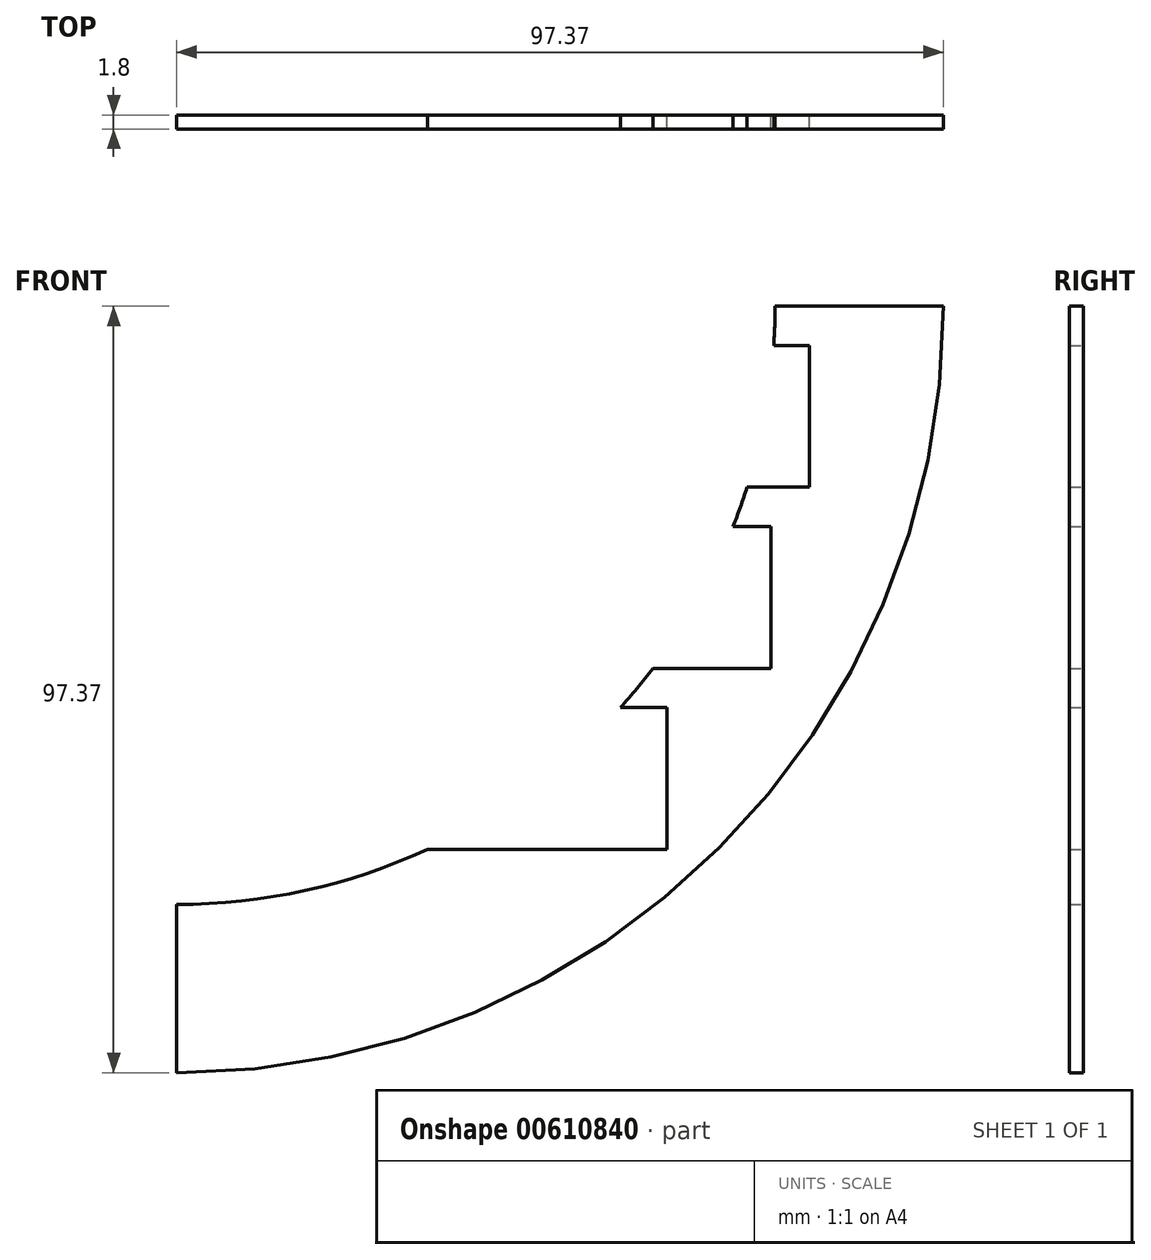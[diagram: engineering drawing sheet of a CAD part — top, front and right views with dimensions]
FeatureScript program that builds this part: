
annotation { "Feature Type Name" : "Feature", "Feature Type Description" : "" }
export const myFeature = defineFeature(function(context is Context, id is Id, definition is map)
    precondition{}
    {
        {
            var Q0;
            Q0=qCreatedBy(makeId("Front.planeOp"),FACE);
            var sketch = newSketch(context, id + "F0", { "sketchPlane" : qUnion([Q0])});
            skArc(sketch, "E0", {"start": v(0, -76) * mm, "mid": v(16.3, -74.23) * mm, "end": v(31.86, -69) * mm});
            skLineSegment(sketch, "E1", {"start": v(0, 0) * mm, "end": v(85, 0) * mm});
            skLineSegment(sketch, "E2", {"start": v(0, 0) * mm, "end": v(0, -85) * mm});
            skLineSegment(sketch, "E3", {"start": v(0, 0) * mm, "end": v(0, -5) * mm});
            skLineSegment(sketch, "E4", {"start": v(0, -5) * mm, "end": v(0, -23) * mm});
            skLineSegment(sketch, "E5", {"start": v(0, -23) * mm, "end": v(0, -28) * mm});
            skLineSegment(sketch, "E6", {"start": v(0, -28) * mm, "end": v(0, -46) * mm});
            skLineSegment(sketch, "E7", {"start": v(0, -46) * mm, "end": v(0, -51) * mm});
            skLineSegment(sketch, "E8", {"start": v(0, -51) * mm, "end": v(0, -69) * mm});
            skLineSegment(sketch, "E9", {"start": v(0, -51) * mm, "end": v(26.66, -51) * mm, "construction": true});
            skLineSegment(sketch, "E10", {"start": v(90.88, -51) * mm, "end": v(90.88, -69) * mm, "construction": true});
            skLineSegment(sketch, "E11", {"start": v(90.88, -69) * mm, "end": v(31.86, -69) * mm, "construction": true});
            skLineSegment(sketch, "E12", {"start": v(0, -28) * mm, "end": v(46.29, -28) * mm, "construction": true});
            skLineSegment(sketch, "E13", {"start": v(107.6, -28) * mm, "end": v(107.6, -46) * mm, "construction": true});
            skLineSegment(sketch, "E14", {"start": v(107.6, -46) * mm, "end": v(60.5, -46) * mm, "construction": true});
            skLineSegment(sketch, "E15", {"start": v(0, -5) * mm, "end": v(49.7, -5) * mm, "construction": true});
            skLineSegment(sketch, "E16", {"start": v(121.2, -5) * mm, "end": v(121.2, -23) * mm, "construction": true});
            skLineSegment(sketch, "E17", {"start": v(121.2, -23) * mm, "end": v(72.44, -23) * mm, "construction": true});
            skCircle(sketch, "E18", {"center": v(0, 0) * mm, "radius": 80.5 * mm, "construction": true});
            skLineSegment(sketch, "E19.bottom", {"start": v(80.34, -5) * mm, "end": v(75.84, -5) * mm});
            skLineSegment(sketch, "E19.top", {"start": v(80.34, -23) * mm, "end": v(72.44, -23) * mm});
            skLineSegment(sketch, "E19.left", {"start": v(80.34, -5) * mm, "end": v(80.34, -23) * mm});
            skLineSegment(sketch, "E20.bottom", {"start": v(75.47, -28) * mm, "end": v(46.29, -28) * mm});
            skLineSegment(sketch, "E20.top", {"start": v(75.47, -46) * mm, "end": v(46.29, -46) * mm});
            skLineSegment(sketch, "E20.left", {"start": v(75.47, -28) * mm, "end": v(75.47, -46) * mm});
            skLineSegment(sketch, "E21.bottom", {"start": v(62.28, -51) * mm, "end": v(56.35, -51) * mm});
            skLineSegment(sketch, "E21.top", {"start": v(62.28, -69) * mm, "end": v(31.86, -69) * mm});
            skLineSegment(sketch, "E21.left", {"start": v(62.28, -51) * mm, "end": v(62.28, -69) * mm});
            skArc(sketch, "E22", {"start": v(0, -97.37) * mm, "mid": v(68.85, -68.85) * mm, "end": v(97.37, 0) * mm});
            skLineSegment(sketch, "E23", {"start": v(0, 0) * mm, "end": v(97.37, 0) * mm});
            skLineSegment(sketch, "E24", {"start": v(0, -85) * mm, "end": v(0, -97.37) * mm});
            skLineSegment(sketch, "E25.trimOffspring", {"start": v(75.84, -5) * mm, "end": v(121.2, -5) * mm, "construction": true});
            skArc(sketch, "E26.trimOffspring", {"start": v(75.84, -5) * mm, "mid": v(75.96, -2.5) * mm, "end": v(76, 0) * mm});
            skLineSegment(sketch, "E27.trimOffspring", {"start": v(49.7, -23) * mm, "end": v(0, -23) * mm, "construction": true});
            skLineSegment(sketch, "E28.trimOffspring", {"start": v(70.65, -28) * mm, "end": v(107.6, -28) * mm, "construction": true});
            skArc(sketch, "E29.trimOffspring", {"start": v(70.65, -28) * mm, "mid": v(71.59, -25.52) * mm, "end": v(72.44, -23) * mm});
            skLineSegment(sketch, "E30.trimOffspring", {"start": v(46.29, -46) * mm, "end": v(0, -46) * mm, "construction": true});
            skLineSegment(sketch, "E31.trimOffspring", {"start": v(56.35, -51) * mm, "end": v(90.88, -51) * mm, "construction": true});
            skArc(sketch, "E32.trimOffspring", {"start": v(56.35, -51) * mm, "mid": v(58.48, -48.54) * mm, "end": v(60.5, -46) * mm});
            skLineSegment(sketch, "E33.trimOffspring", {"start": v(26.66, -69) * mm, "end": v(0, -69) * mm, "construction": true});
            skLineSegment(sketch, "E34", {"start": v(62.28, -60) * mm, "end": v(70.49, -60) * mm, "construction": true});
            skLineSegment(sketch, "E35", {"start": v(75.47, -37) * mm, "end": v(83.26, -37) * mm, "construction": true});
            skLineSegment(sketch, "E36", {"start": v(80.34, -14) * mm, "end": v(86.94, -14) * mm, "construction": true});
            skPoint(sketch, "E36.endSnap0", {"position": v(80.34, -14) * mm});
            skSolve(sketch);
        }
        {
            var Q0;
            {var subQ3=sQuery(id+"F0.wireOp",EDGE,"E0");Q0=makeQuery(id+"F0.imprint","IMPRINT",FACE,{"disambiguationData":[TD([[makeQuery(id+"F0.imprint","IMPRINT",EDGE,{"derivedFrom":subQ3}),-1.0]])]});}
            extrude(context, id + "F1", {"entities" : qUnion([Q0]), "depth" : 1.8 * mm, "offsetDistance" : 25 * mm});
        }
    });
